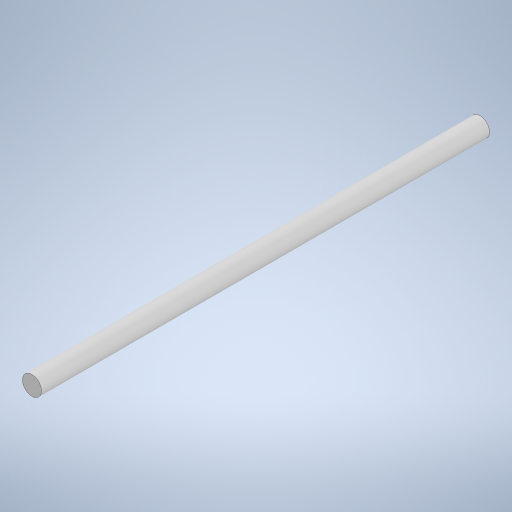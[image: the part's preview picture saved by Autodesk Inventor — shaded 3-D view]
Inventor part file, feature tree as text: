
AUTODESK INVENTOR PART (.ipt)
format: ipt  version: 2024 (Build 280153000, 153)  size: 231,424 bytes
history: native  units: mm
features: extrude x1, sketch x1
ambient origin geometry x8: Origin, YZ Plane, XZ Plane, XY Plane, X Axis, Y Axis, Z Axis, Center Point
bodies: Solid1 (feature_tree)
feature tree (2):
  extrude  "Extrusion1"  Depth=300.0mm TaperAngle=0.0deg
  sketch  "Sketch1"  dims[d0=12.7mm d1=300.0mm d2=0.0mm]
